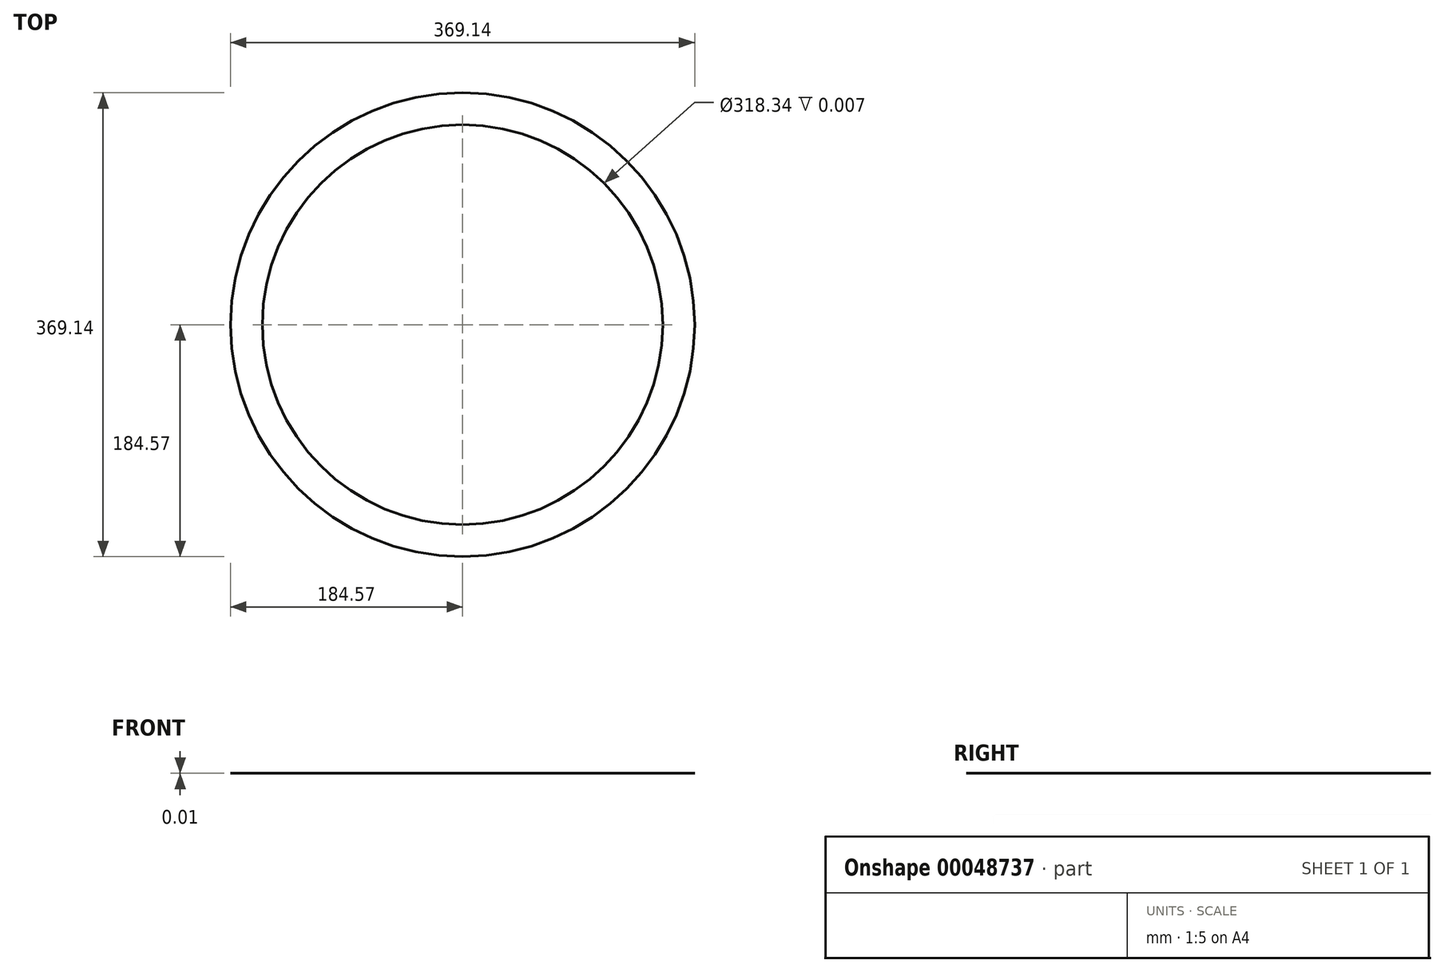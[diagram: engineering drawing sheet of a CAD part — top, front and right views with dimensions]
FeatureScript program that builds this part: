
annotation { "Feature Type Name" : "Feature", "Feature Type Description" : "" }
export const myFeature = defineFeature(function(context is Context, id is Id, definition is map)
    precondition{}
    {
        {
            var Q0;
            Q0=qCreatedBy(makeId("Top.planeOp"),FACE);
            var sketch = newSketch(context, id + "F0", { "sketchPlane" : qUnion([Q0])});
            skCircle(sketch, "E0", {"center": v(0, 0) * mm, "radius": 184.57 * mm});
            skCircle(sketch, "E1", {"center": v(0, 0) * mm, "radius": 159.17 * mm});
            skSolve(sketch);
        }
        {
            var Q0;
            Q0=makeQuery(id+"F0.imprint","IMPRINT",FACE,{"disambiguationData":[TD([[makeQuery(id+"F0.imprint","IMPRINT",EDGE,{"derivedFrom":sQuery(id+"F0.wireOp",EDGE,"E0")}),1.0]])]});
            extrude(context, id + "F1", {"entities" : qUnion([Q0]), "depth" : 3 / 406.4 * mm});
        }
    });
